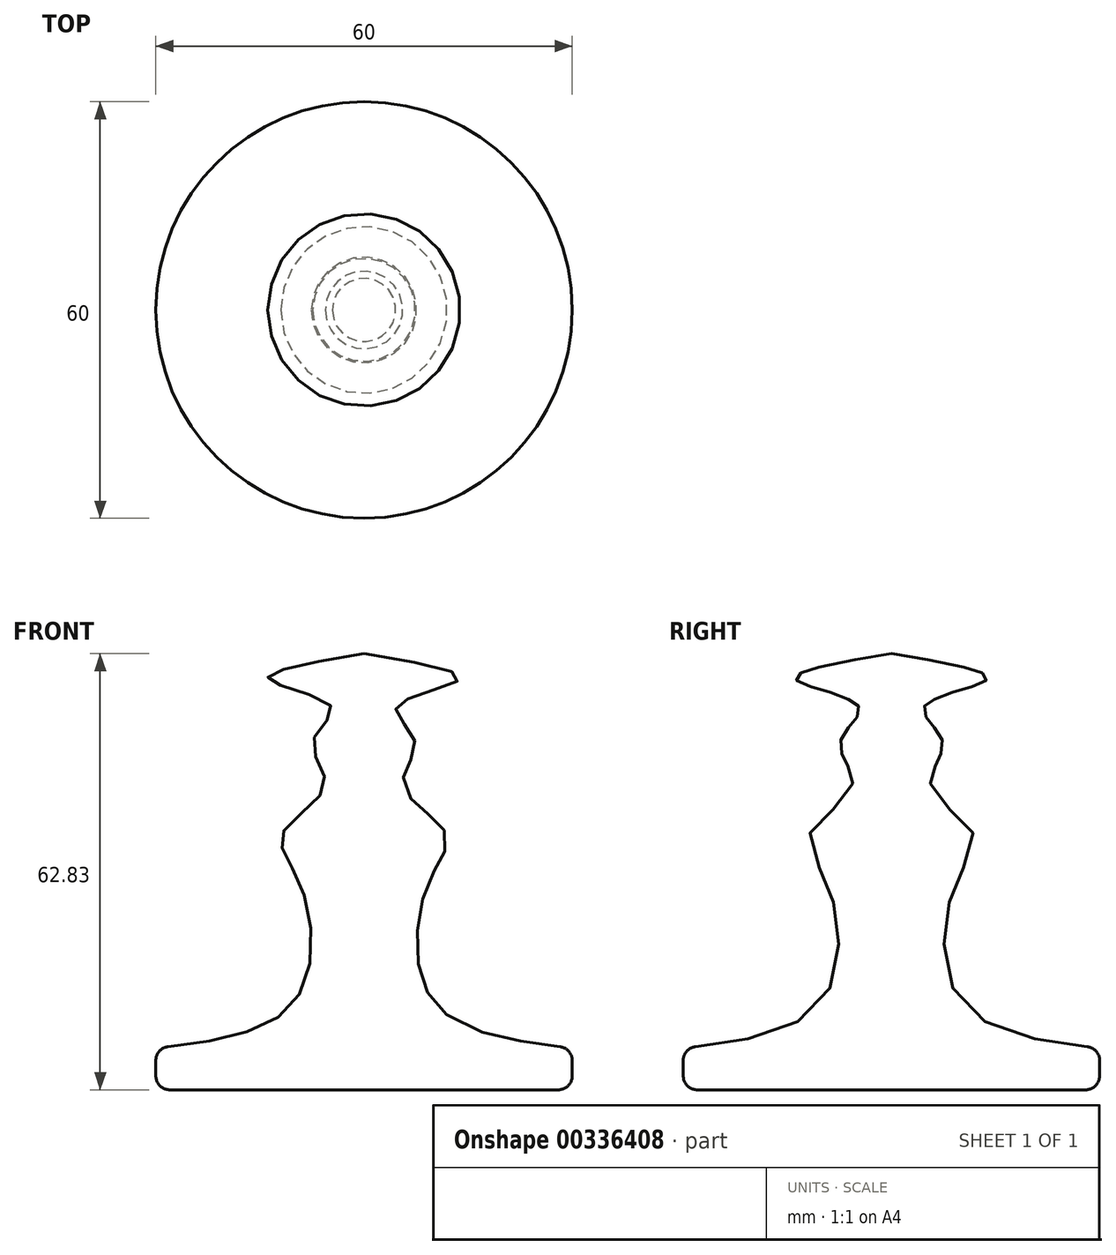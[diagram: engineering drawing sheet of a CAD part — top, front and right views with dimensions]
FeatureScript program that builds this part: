
annotation { "Feature Type Name" : "Feature", "Feature Type Description" : "" }
export const myFeature = defineFeature(function(context is Context, id is Id, definition is map)
    precondition{}
    {
        {
            var Q0;
            Q0=qCreatedBy(makeId("Front.planeOp"),FACE);
            var sketch = newSketch(context, id + "F0", { "sketchPlane" : qUnion([Q0])});
            skLineSegment(sketch, "E0", {"start": v(0, -62.83) * mm, "end": v(-30, -62.83) * mm});
            skLineSegment(sketch, "E1", {"start": v(-30, -62.83) * mm, "end": v(-30, -56.83) * mm});
            skFitSpline(sketch, "E2", {"points": [v(-30, -56.83) * mm, v(-9.8, -49.87) * mm, v(-9.31, -32.96) * mm, v(-11.76, -25.85) * mm, v(-5.64, -19) * mm, v(-7.35, -12.62) * mm, v(-4.66, -7.72) * mm, v(-13.72, -3.8) * mm, v(0, 0) * mm], "startDerivative": vector(142.4, 16.69) * mm, "endDerivative": vector(157.19, 26.33) * mm});
            skLineSegment(sketch, "E3", {"start": v(0, 0) * mm, "end": v(0, -62.83) * mm});
            skSolve(sketch);
        }
        {
            var Q0;
            Q0=makeQuery(id+"F0.imprint","IMPRINT",FACE,{"disambiguationData":[TD([[makeQuery(id+"F0.imprint","IMPRINT",EDGE,{"derivedFrom":sQuery(id+"F0.wireOp",EDGE,"E0")}),-1.0]])]});
            var Q1;
            Q1=sQuery(id+"F0.wireOp",EDGE,"E3");
            revolve(context, id + "F1", {"entities" : qUnion([Q0]), "axis" : qUnion([Q1]), "revolveType" : RevolveType.FULL});
        }
        {
            var Q0;
            Q0=makeQuery(id+"F1.opRevolve","SWEPT_FACE",FACE,{"disambiguationData":[OSD([sQuery(id+"F0.wireOp",EDGE,"E2")])]});
            var Q1;
            Q1=makeQuery(id+"F1.opRevolve","SWEPT_FACE",FACE,{"disambiguationData":[OSD([sQuery(id+"F0.wireOp",EDGE,"E1")])]});
            fillet(context, id + "F2", {"entities" : qUnion([Q0, Q1]), "radius" : 2 * mm, "tangentPropagation" : true, "allowEdgeOverflow" : false});
        }
    });
